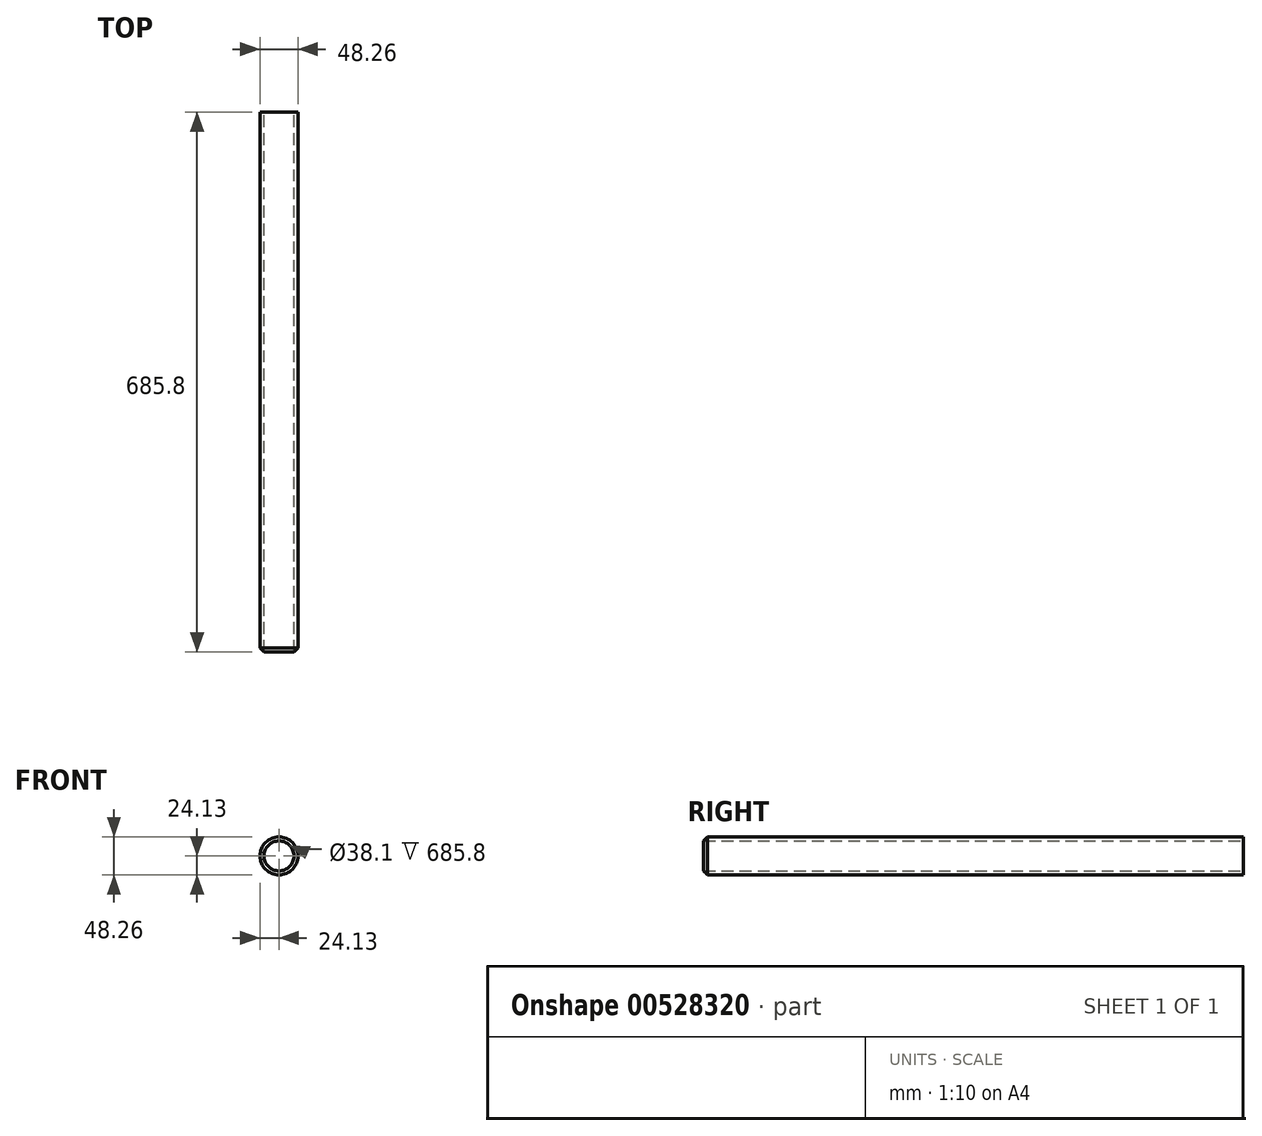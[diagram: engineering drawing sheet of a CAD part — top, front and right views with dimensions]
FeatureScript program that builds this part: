
annotation { "Feature Type Name" : "Feature", "Feature Type Description" : "" }
export const myFeature = defineFeature(function(context is Context, id is Id, definition is map)
    precondition{}
    {
        {
            var Q0;
            Q0=qCreatedBy(makeId("Front.planeOp"),FACE);
            var sketch = newSketch(context, id + "F0", { "sketchPlane" : qUnion([Q0])});
            skCircle(sketch, "E0", {"center": v(0, 0) * mm, "radius": 19.05 * mm});
            skCircle(sketch, "E1", {"center": v(0, 0) * mm, "radius": 24.13 * mm});
            skSolve(sketch);
        }
        {
            var Q0;
            Q0 = qSketchRegion(id + "F0", true);
            extrude(context, id + "F1", {"entities" : qUnion([Q0]), "depth" : 228.6 * mm, "offsetDistance" : 25.4 * mm, "hasSecondDirection" : true, "secondDirectionOppositeDirection" : true, "secondDirectionDepth" : 457.2 * mm});
        }
        {
            var Q0;
            Q0=makeQuery(id+"F1.opExtrude","CAP_EDGE",EDGE,{"disambiguationData":[OSD([sQuery(id+"F0.wireOp",EDGE,"E1")])],"isStart":false});
            chamfer(context, id + "F2", {"entities" : qUnion([Q0]), "width" : 5.08 * mm, "tangentPropagation" : true});
        }
    });
